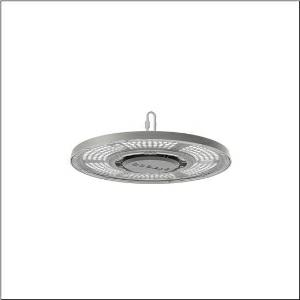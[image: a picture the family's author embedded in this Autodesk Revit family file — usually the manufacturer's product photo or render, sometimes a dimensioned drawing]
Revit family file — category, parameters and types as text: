
# Revit family: highbay_31-l_51hc42da4jmb
name_source: partatom
category: Lighting Fixtures
units: mm (PartAtom-declared; Revit-internal decimal feet)

## family parameters
Cut with Voids When Loaded = No
Host = Face
Light Source = No
Part Type = Normal
Room Calculation Point = No
Round Connector Dimension = Use Diameter
Shared = No

## types (1)
- Highbay 31-L (1 x LED, 20000 lm, 134 W, 4000K)
    Apparent Load = 134 VA
    CIE Flux Codes = 77 99 100 100 100
    Color Rendering = 80
    Color Temperature = 4000K
    Default Elevation = 1800 mm
    Description = Highbay 31-L, LED high bay luminaire, primary light control with lens, of PC, primary optical cover: cover panel, of PC, transparent, light emission: direct distribution, primary light characteristic: rotationally symmetric, installation type: suspended mounting, surface-mounted, LED, rated luminous flux: 20.000lm, luminous efficacy: 150lm/W, light colour: 840, colour temperature: 4000K, control gear: ECG DALI, with cable, 5x 1.0mm², free wire ends, mains connection: 220..240V, AC/DC, 0/50..60Hz, cable length: 1,5m, rated input power: 134W, housing, rotationally symmetric, of diecast aluminium, grey aluminium (RAL 9007), diameter: 404mm, protection rating (complete): IP65, insulation class (complete): insulation class I (protective earthing), certification: CE, ENEC, UKCA, protection symbol: D, impact resistance: IK08, permissible operating ambient temperature: -30..+45°C, standard: EN 60598-2-22, EN 60598, corresponds to IFS (International Featured Standards) requirements for safety and quality in the food industry, packaging unit: 1 piece
    Height = 141 mm
    Lamp = 1 x LED
    Lamp Light Flux = 20000 lm
    Lamp Power = 134 W
    Lamp count = 1
    Length = 406 mm
    Luminous efficacy = 149 lm/W
    Manufacturer = Siteco
    ModVariant = No
    Model = 51HC42DA4JMB
    Mounting Place = Ceiling
    Mounting Type = Pendant
    Number of Poles = 1
    OnlyDefault = Yes
    Power Factor = 1
    Product Name = Highbay 31-L
    Product group = LED high bay luminaire
    ProductGroupID = 903
    Protection Class = Protection class I
    Protection Degree = IP 65
    RLX_Detail_Level = 1
    RlxData = <blob elided: 162705 chars, md5=80779b5d>
    Socket = socket
    Standby Power = 0 W
    System Light Flux = 20000 lm
    System Power = 134 W
    Type Comments = Product without accessories
    Type Image = l_1007237.jpg
    URL = http://relux.com
    VarID = ---
    Voltage = 0 V
    Weight = 0.00 kg
    Width = 0 mm  [stored 0 ft]

note: [stored X ft] marks values corroborated as IEEE doubles in the binary element streams (Revit-internal decimal feet)

## geometry (parser evidence)
native form markers: Blend x4, Sweep x11
no freeform markers — native parametric forms only
